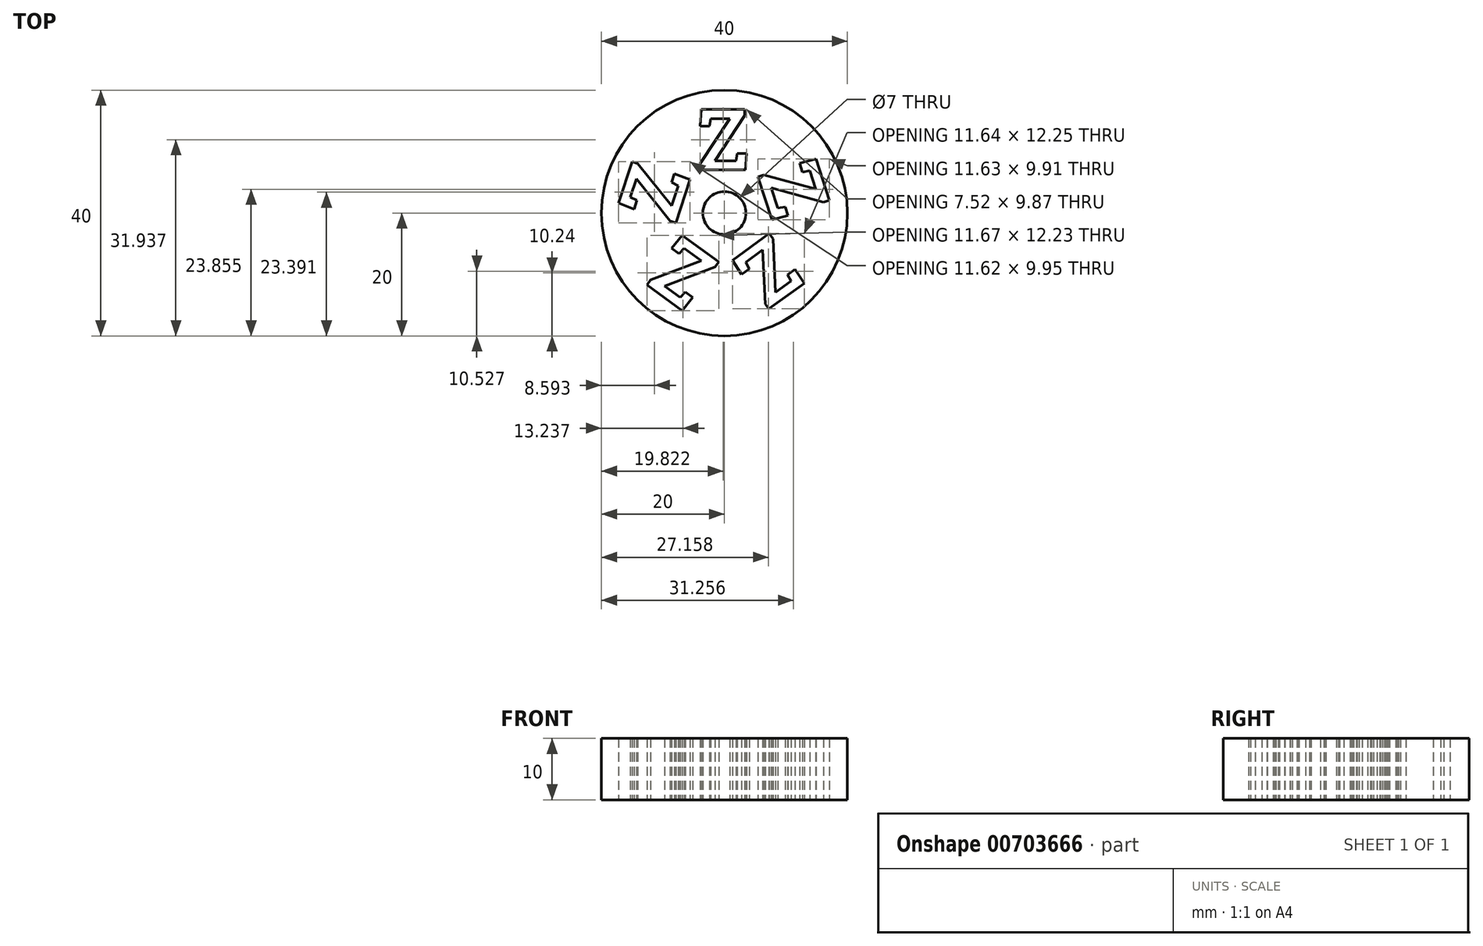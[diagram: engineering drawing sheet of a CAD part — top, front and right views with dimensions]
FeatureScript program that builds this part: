
annotation { "Feature Type Name" : "Feature", "Feature Type Description" : "" }
export const myFeature = defineFeature(function(context is Context, id is Id, definition is map)
    precondition{}
    {
        {
            var Q0;
            Q0=qCreatedBy(makeId("Top.planeOp"),FACE);
            var sketch = newSketch(context, id + "F0", { "sketchPlane" : qUnion([Q0])});
            skCircle(sketch, "E0", {"center": v(0, 0) * mm, "radius": 20 * mm});
            skSolve(sketch);
        }
        {
            var Q0;
            Q0 = qSketchRegion(id + "F0", true);
            extrude(context, id + "F1", {"entities" : qUnion([Q0]), "depth" : 10 * mm, "offsetDistance" : 25 * mm});
        }
        {
            var Q0;
            Q0=qCreatedBy(makeId("Top.planeOp"),FACE);
            var sketch = newSketch(context, id + "F2", { "sketchPlane" : qUnion([Q0])});
            skText(sketch, "E1", { "text": "Z", "fontName": "RobotoSlab-Bold.ttf"});
            skLineSegment(sketch, "E2", {"start": v(0, 0) * mm, "end": v(0, 17) * mm, "construction": true});
            skCircle(sketch, "E3", {"center": v(0, 0) * mm, "radius": 3.5 * mm});
            const initialGuessF2  = {"E1": [-0.00444, 0.007, 1, 0, 0.01]};
            skSetInitialGuess(sketch, initialGuessF2);
            skSolve(sketch);
        }
        {
            var Q0;
            Q0=qCreatedBy(makeId("Right.planeOp"),FACE);
            var sketch = newSketch(context, id + "F3", { "sketchPlane" : qUnion([Q0])});
            skLineSegment(sketch, "E4", {"start": v(0, 0) * mm, "end": v(0, 59.62) * mm, "construction": true});
            skSolve(sketch);
        }
        {
            var Q0;
            Q0 = qSketchRegion(id + "F2", true);
            extrude(context, id + "F4", {"entities" : qUnion([Q0]), "depth" : 35 * mm, "offsetDistance" : 25 * mm});
        }
        {
            var Q0;
            Q0=makeQuery(id+"F4.opExtrude","SWEPT_BODY",BODY,{"disambiguationData":[OSD([sQuery(id+"F2.wireOp",EDGE,"E1.sketch_text.stroke-0"),sQuery(id+"F2.wireOp",EDGE,"E1.sketch_text.stroke-1"),sQuery(id+"F2.wireOp",EDGE,"E1.sketch_text.stroke-2"),sQuery(id+"F2.wireOp",EDGE,"E1.sketch_text.stroke-3"),sQuery(id+"F2.wireOp",EDGE,"E1.sketch_text.stroke-4"),sQuery(id+"F2.wireOp",EDGE,"E1.sketch_text.stroke-5"),sQuery(id+"F2.wireOp",EDGE,"E1.sketch_text.stroke-6"),sQuery(id+"F2.wireOp",EDGE,"E1.sketch_text.stroke-7"),sQuery(id+"F2.wireOp",EDGE,"E1.sketch_text.stroke-8"),sQuery(id+"F2.wireOp",EDGE,"E1.sketch_text.stroke-9"),sQuery(id+"F2.wireOp",EDGE,"E1.sketch_text.stroke-10"),sQuery(id+"F2.wireOp",EDGE,"E1.sketch_text.stroke-11"),sQuery(id+"F2.wireOp",EDGE,"E1.sketch_text.stroke-12"),sQuery(id+"F2.wireOp",EDGE,"E1.sketch_text.stroke-13")])]});
            var Q1;
            Q1=makeQuery(id+"F4.opExtrude","SWEPT_BODY",BODY,{"disambiguationData":[OSD([sQuery(id+"F2.wireOp",EDGE,"E3")])]});
            var Q2;
            Q2=sQuery(id+"F3.wireOp",EDGE,"E4");
            circularPattern(context, id + "F5", {"operationType" : NewBodyOperationType.REMOVE, "entities" : qUnion([Q0, Q1]), "axis" : qUnion([Q2]), "angle" : 360 * degree, "instanceCount" : 5, "equalSpace" : true});
        }
    });
